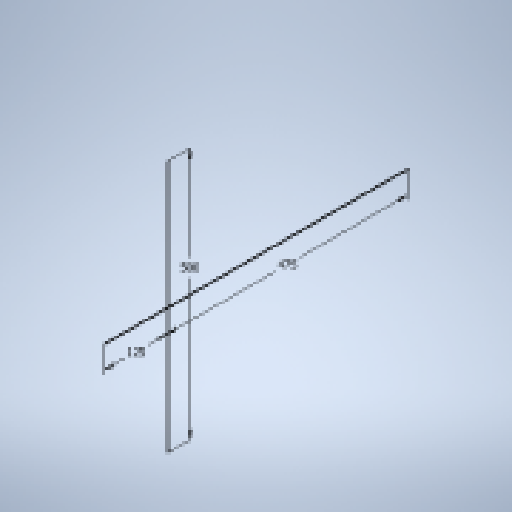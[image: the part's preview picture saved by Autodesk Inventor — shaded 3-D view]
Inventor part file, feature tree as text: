
AUTODESK INVENTOR PART (.ipt)
format: ipt  version: 2024 (Build 280153000, 153)  size: 127,488 bytes
history: native  units: in
note: dims shown in document units (in); Inventor stores cm internally (conversion verified against a paired STEP export)
features: sketch x1
ambient origin geometry x8: Origin, YZ Plane, XZ Plane, XY Plane, X Axis, Y Axis, Z Axis, Center Point
feature tree (1):
  sketch  "Sketch1"  dims[d0=19.685in d1=18.7008in d2=4.9213in]
